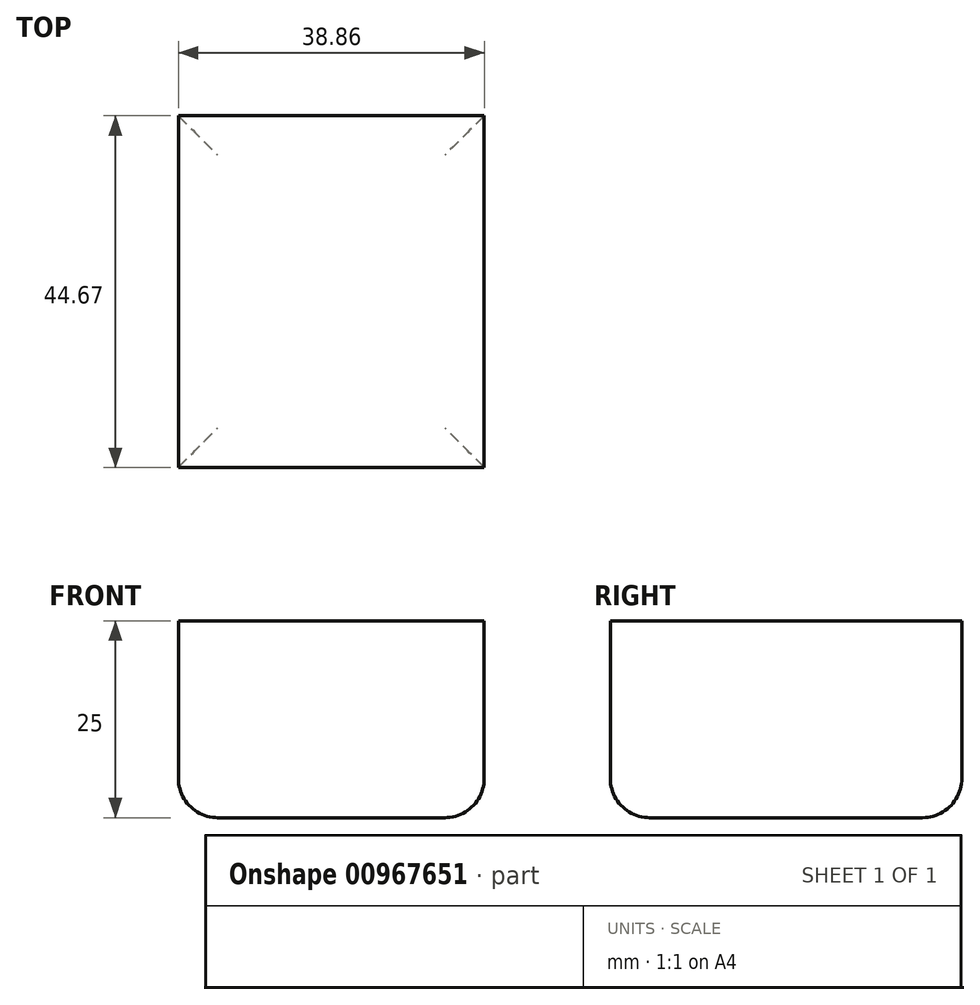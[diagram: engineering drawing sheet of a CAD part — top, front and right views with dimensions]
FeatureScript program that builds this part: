
annotation { "Feature Type Name" : "Feature", "Feature Type Description" : "" }
export const myFeature = defineFeature(function(context is Context, id is Id, definition is map)
    precondition{}
    {
        {
            var Q0;
            Q0=qCreatedBy(makeId("Top.planeOp"),FACE);
            var sketch = newSketch(context, id + "F0", { "sketchPlane" : qUnion([Q0])});
            skLineSegment(sketch, "E0", {"start": v(0, 0) * mm, "end": v(0, -44.67) * mm});
            skLineSegment(sketch, "E1", {"start": v(0, -44.67) * mm, "end": v(38.86, -44.67) * mm});
            skLineSegment(sketch, "E2", {"start": v(38.86, -44.67) * mm, "end": v(38.86, 0) * mm});
            skLineSegment(sketch, "E3", {"start": v(38.86, 0) * mm, "end": v(0, 0) * mm});
            skSolve(sketch);
        }
        {
            var Q0;
            Q0 = qSketchRegion(id + "F0", true);
            var Q1;
            Q1=makeQuery(id+"F0.imprint","IMPRINT",FACE,{"disambiguationData":[TD([[makeQuery(id+"F0.imprint","IMPRINT",EDGE,{"derivedFrom":sQuery(id+"F0.wireOp",EDGE,"E0")}),1.0]])]});
            extrude(context, id + "F1", {"entities" : qUnion([Q0, Q1]), "depth" : 25 * mm, "offsetDistance" : 25 * mm});
        }
        {
            var Q0;
            Q0=makeQuery(id+"F1.opExtrude","CAP_EDGE",EDGE,{"disambiguationData":[OSD([sQuery(id+"F0.wireOp",EDGE,"E1")])],"isStart":true});
            var Q1;
            Q1=makeQuery(id+"F1.opExtrude","CAP_EDGE",EDGE,{"disambiguationData":[OSD([sQuery(id+"F0.wireOp",EDGE,"E2")])],"isStart":true});
            var Q2;
            Q2=makeQuery(id+"F1.opExtrude","CAP_EDGE",EDGE,{"disambiguationData":[OSD([sQuery(id+"F0.wireOp",EDGE,"E3")])],"isStart":true});
            var Q3;
            Q3=makeQuery(id+"F1.opExtrude","CAP_EDGE",EDGE,{"disambiguationData":[OSD([sQuery(id+"F0.wireOp",EDGE,"E0")])],"isStart":true});
            fillet(context, id + "F2", {"entities" : qUnion([Q0, Q1, Q2, Q3]), "radius" : 5 * mm, "tangentPropagation" : true, "allowEdgeOverflow" : false});
        }
    });
